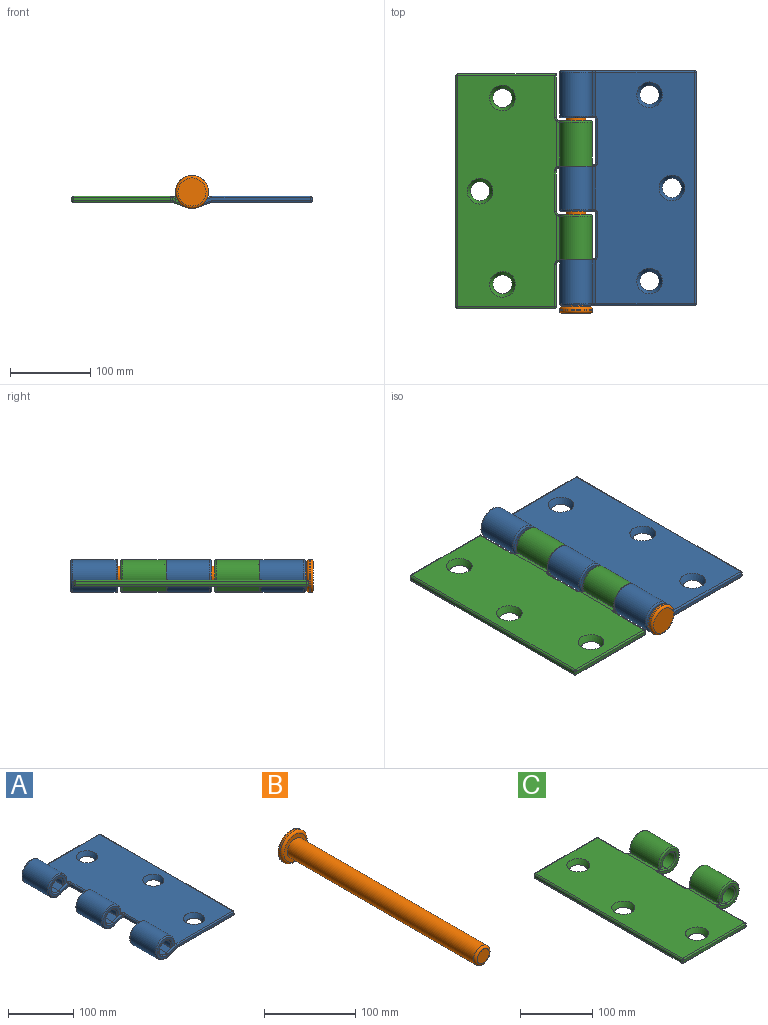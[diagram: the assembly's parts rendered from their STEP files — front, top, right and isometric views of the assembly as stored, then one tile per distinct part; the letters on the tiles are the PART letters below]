
ASSEMBLY  parts=3 mates=2
PART A: 95 faces, bbox 171.7x292x44.4 mm
  f0: plane 54.63x17.59mm, normal (0.34,0,-0.94), area 1016.4mm2, adj f2,f12,f42,f44,f80
  f1: plane 54.85x17.59mm, normal (0.34,0,-0.94), area 1016.5mm2, adj f3,f12,f51,f52,f62,f64
  f2: cylinder r=20.5mm len=54.4mm, axis (0,1,0), area 5913.6mm2, adj f0,f4,f40,f81
  f3: cylinder r=20.5mm len=54.4mm, axis (0,1,0), area 5913.6mm2, adj f1,f5,f49,f60
  f4: plane 54.4x8.42mm, normal (0,0,-1), area 458.3mm2, adj f2,f6,f38,f86
  f5: plane 54.4x8.42mm, normal (0,0,-1), area 458.3mm2, adj f3,f7,f47,f58
  f6: cylinder r=12.5mm len=54.4mm, axis (0,1,0), area 3703.3mm2, adj f4,f8,f36,f89
  f7: cylinder r=12.5mm len=54.4mm, axis (0,1,0), area 3703.3mm2, adj f5,f9,f45,f56
  f8: plane 55.3x20.54mm, normal (-0.32,0,0.95), area 1179mm2, adj f6,f10,f33,f34,f35,f92
  f9: plane 56.21x20.54mm, normal (-0.32,0,0.95), area 1179.8mm2, adj f7,f10,f39,f41,f43,f53,f54,f55
  f10: plane 288x123mm, normal (0,0,1), area 32774mm2, adj f8,f9,f17,f20,f21,f22,f35,f37
  f11: plane 288x4mm, normal (1,0,0), area 1152mm2, adj f83,f84,f90,f91
  f12: plane 288x123.06mm, normal (0,0,-1), area 33829.6mm2, adj f0,f1,f13,f20,f21,f22,f44,f46
  f13: plane 54.63x17.59mm, normal (0.34,0,-0.94), area 1016.4mm2, adj f12,f14,f71,f72,f75
  f14: cylinder r=20.5mm len=54.4mm, axis (0,1,0), area 5913.6mm2, adj f13,f15,f69,f73
  f15: plane 54.4x8.42mm, normal (0,0,-1), area 458.3mm2, adj f14,f16,f67,f74
  f16: cylinder r=12.5mm len=54.4mm, axis (0,1,0), area 3703.3mm2, adj f15,f17,f65,f76
  f17: plane 55.3x20.54mm, normal (-0.32,0,0.95), area 1179mm2, adj f10,f16,f59,f61,f63,f78
  f18: plane 166x37mm, normal (0,-1,0), area 913.5mm2, adj f80,f81,f85,f86,f89,f91,f92,f94
  f19: plane 166x37mm, normal (0,1,0), area 913.5mm2, adj f73,f74,f75,f76,f77,f78,f82,f83
  f20: cone r=16mm half-angle=26.6deg, axis (0,0,1), area 786.8mm2, adj f10,f12
  f21: cone r=16mm half-angle=26.6deg, axis (0,0,1), area 786.8mm2, adj f10,f12
  f22: cone r=16mm half-angle=26.6deg, axis (0,0,1), area 786.8mm2, adj f10,f12
  f23: plane 41x37mm, normal (0,1,0), area 413.9mm2, adj f29,f54,f56,f58,f60,f62
  f24: plane 54.4x4mm, normal (-1,0,0), area 217.6mm2, adj f29,f30,f57,f68
  f25: plane 41x37mm, normal (0,-1,0), area 413.9mm2, adj f30,f63,f65,f67,f69,f71
  f26: plane 41x37mm, normal (0,1,0), area 413.9mm2, adj f31,f34,f36,f38,f40,f42
  f27: plane 54.4x4mm, normal (-1,0,0), area 217.6mm2, adj f31,f32,f37,f48
  f28: plane 41x37mm, normal (0,-1,0), area 413.9mm2, adj f32,f43,f45,f47,f49,f51
  f29: cylinder r=2mm len=4.59mm, axis (0,0,1), area 12.3mm2, adj f23,f24,f53,f55,f64,f66
  f30: cylinder r=2mm len=4.59mm, axis (0,0,-1), area 12.3mm2, adj f24,f25,f59,f61,f70,f72
  f31: cylinder r=2mm len=4.59mm, axis (0,0,1), area 12.3mm2, adj f26,f27,f33,f35,f44,f46
  f32: cylinder r=2mm len=4.59mm, axis (0,0,-1), area 12.3mm2, adj f27,f28,f39,f41,f50,f52
  f33: bspline ~2.75x2.54mm, area 6mm2, adj f8,f31,f34,f35
  f34: cylinder r=2mm len=18.54mm, axis (-0.95,0,-0.32), area 59.3mm2, adj f8,f26,f33,f36
  f35: torus R=4mm, axis (0,0,-1), area 8.7mm2, adj f8,f10,f31,f33,f37
  f36: torus R=14.5mm, axis (0,1,0), area 222mm2, adj f6,f26,f34,f38
  f37: cylinder r=2mm len=54.4mm, axis (0,1,0), area 170.9mm2, adj f10,f27,f35,f39
  f38: cylinder r=2mm len=8.42mm, axis (1,0,0), area 19.6mm2, adj f4,f26,f36,f40
  f39: torus R=4mm, axis (0,0,-1), area 8.7mm2, adj f9,f10,f32,f37,f41
  f40: torus R=18.5mm, axis (0,1,0), area 326.9mm2, adj f2,f26,f38,f42
  f41: bspline ~3.65x3.11mm, area 6mm2, adj f9,f32,f39,f43
  f42: cylinder r=2mm len=16.94mm, axis (0.94,0,0.34), area 54.3mm2, adj f0,f26,f40,f44
  f43: cylinder r=2mm len=18.54mm, axis (0.95,0,0.32), area 59.3mm2, adj f9,f28,f41,f45
  f44: bspline ~2.47x2.33mm, area 3.5mm2, adj f0,f12,f31,f42,f46
  f45: torus R=14.5mm, axis (0,1,0), area 222mm2, adj f7,f28,f43,f47
  f46: torus R=4mm, axis (0,0,-1), area 9.2mm2, adj f12,f31,f44,f48
  f47: cylinder r=2mm len=8.42mm, axis (-1,0,0), area 19.6mm2, adj f5,f28,f45,f49
  f48: cylinder r=2mm len=54.4mm, axis (0,-1,0), area 170.9mm2, adj f12,f27,f46,f50
  f49: torus R=18.5mm, axis (0,1,0), area 326.9mm2, adj f3,f28,f47,f51
  f50: torus R=4mm, axis (0,0,-1), area 9.2mm2, adj f12,f32,f48,f52
  f51: cylinder r=2mm len=16.94mm, axis (-0.94,0,-0.34), area 54.3mm2, adj f1,f28,f49,f52
  f52: bspline ~2.47x2.33mm, area 3.5mm2, adj f1,f12,f32,f50,f51
  f53: bspline ~2.75x2.54mm, area 6mm2, adj f9,f29,f54,f55
  f54: cylinder r=2mm len=18.54mm, axis (-0.95,0,-0.32), area 59.3mm2, adj f9,f23,f53,f56
  f55: torus R=4mm, axis (0,0,-1), area 8.7mm2, adj f9,f10,f29,f53,f57
  f56: torus R=14.5mm, axis (0,1,0), area 222mm2, adj f7,f23,f54,f58
  f57: cylinder r=2mm len=54.4mm, axis (0,1,0), area 170.9mm2, adj f10,f24,f55,f59
  f58: cylinder r=2mm len=8.42mm, axis (1,0,0), area 19.6mm2, adj f5,f23,f56,f60
  f59: torus R=4mm, axis (0,0,-1), area 8.7mm2, adj f10,f17,f30,f57,f61
  f60: torus R=18.5mm, axis (0,1,0), area 326.9mm2, adj f3,f23,f58,f62
  f61: bspline ~3.65x3.11mm, area 6mm2, adj f17,f30,f59,f63
  f62: cylinder r=2mm len=16.94mm, axis (0.94,0,0.34), area 54.3mm2, adj f1,f23,f60,f64
  f63: cylinder r=2mm len=18.54mm, axis (0.95,0,0.32), area 59.3mm2, adj f17,f25,f61,f65
  f64: bspline ~2.47x2.33mm, area 3.5mm2, adj f1,f12,f29,f62,f66
  f65: torus R=14.5mm, axis (0,1,0), area 222mm2, adj f16,f25,f63,f67
  f66: torus R=4mm, axis (0,0,-1), area 9.2mm2, adj f12,f29,f64,f68
  f67: cylinder r=2mm len=8.42mm, axis (-1,0,0), area 19.6mm2, adj f15,f25,f65,f69
  f68: cylinder r=2mm len=54.4mm, axis (0,-1,0), area 170.9mm2, adj f12,f24,f66,f70
  f69: torus R=18.5mm, axis (0,1,0), area 326.9mm2, adj f14,f25,f67,f71
  f70: torus R=4mm, axis (0,0,-1), area 9.2mm2, adj f12,f30,f68,f72
  f71: cylinder r=2mm len=16.94mm, axis (-0.94,0,-0.34), area 54.3mm2, adj f13,f25,f69,f72
  f72: bspline ~2.47x2.33mm, area 3.5mm2, adj f12,f13,f30,f70,f71
  f73: torus R=18.5mm, axis (0,-1,0), area 326.9mm2, adj f14,f19,f74,f75
  f74: cylinder r=2mm len=8.42mm, axis (-1,0,0), area 19.6mm2, adj f15,f19,f73,f76
  f75: cylinder r=2mm len=18.59mm, axis (-0.94,0,-0.34), area 59.2mm2, adj f13,f19,f73,f77
  f76: torus R=14.5mm, axis (0,-1,0), area 222mm2, adj f16,f19,f74,f78
  f77: cylinder r=2mm len=123.35mm, axis (-1,0,0), area 387mm2, adj f12,f19,f75,f79
  f78: cylinder r=2mm len=21.18mm, axis (0.95,0,0.32), area 67.5mm2, adj f17,f19,f76,f82
  f79: sphere r=2mm, area 4mm2, adj f77,f83,f84
  f80: cylinder r=2mm len=18.59mm, axis (0.94,0,0.34), area 59.2mm2, adj f0,f18,f81,f85
  f81: torus R=18.5mm, axis (0,-1,0), area 326.9mm2, adj f2,f18,f80,f86
  f82: cylinder r=2mm len=123mm, axis (1,0,0), area 385.9mm2, adj f10,f19,f78,f87
  f83: cylinder r=2mm len=4mm, axis (0,0,-1), area 12.6mm2, adj f11,f19,f79,f87
  f84: cylinder r=2mm len=288mm, axis (0,-1,0), area 904.8mm2, adj f11,f12,f79,f88
  f85: cylinder r=2mm len=123.35mm, axis (1,0,0), area 387mm2, adj f12,f18,f80,f88
  f86: cylinder r=2mm len=8.42mm, axis (1,0,0), area 19.6mm2, adj f4,f18,f81,f89
  f87: sphere r=2mm, area 6.3mm2, adj f82,f83,f90
  f88: sphere r=2mm, area 6.3mm2, adj f84,f85,f91
  f89: torus R=14.5mm, axis (0,-1,0), area 222mm2, adj f6,f18,f86,f92
  f90: cylinder r=2mm len=288mm, axis (0,1,0), area 904.8mm2, adj f10,f11,f87,f93
  f91: cylinder r=2mm len=4mm, axis (0,0,1), area 12.6mm2, adj f11,f18,f88,f93
  f92: cylinder r=2mm len=21.18mm, axis (-0.95,0,-0.32), area 67.5mm2, adj f8,f18,f89,f94
  f93: sphere r=2mm, area 6.3mm2, adj f90,f91,f94
  f94: cylinder r=2mm len=123mm, axis (-1,0,0), area 385.9mm2, adj f10,f18,f92,f93
PART B: 8 faces, bbox 44.4x300x44.4 mm
  f0: cylinder r=12.25mm len=289mm, axis (0,1,0), area 22244mm2, adj f4,f7
  f1: plane 18.5x18.5mm, normal (0,-1,0), area 268.8mm2, adj f7
  f2: cylinder r=20.5mm len=41mm, axis (0,-1,0), area 257.6mm2, adj f5,f6
  f3: plane 35x35mm, normal (0,1,0), area 962.1mm2, adj f6
  f4: plane 35x35mm, normal (0,-1,0), area 490.7mm2, adj f0,f5
  f5: torus R=17.5mm, axis (0,1,0), area 574.7mm2, adj f2,f4
  f6: torus R=17.5mm, axis (0,1,0), area 574.7mm2, adj f2,f3
  f7: torus R=9.25mm, axis (0,1,0), area 330.4mm2, adj f0,f1
PART C: 85 faces, bbox 172x292.3x44.6 mm
  f0: plane 58.5x20.63mm, normal (0.32,0,0.95), area 1184.5mm2, adj f8,f12,f37,f40,f43,f65,f66,f67
  f1: plane 58.5x20.63mm, normal (0.32,0,0.95), area 1184.5mm2, adj f9,f12,f30,f32,f35,f71,f73,f75
  f2: plane 56.41x17.59mm, normal (-0.34,0,-0.94), area 1018.6mm2, adj f4,f14,f63,f64,f74,f76
  f3: plane 56.41x17.59mm, normal (-0.34,0,-0.94), area 1018.6mm2, adj f5,f14,f36,f39,f83,f84
  f4: cylinder r=20.5mm len=54.4mm, axis (0,1,0), area 5913.6mm2, adj f2,f6,f61,f72
  f5: cylinder r=20.5mm len=54.4mm, axis (0,1,0), area 5913.6mm2, adj f3,f7,f33,f81
  f6: plane 56.67x8.7mm, normal (0,0,-1), area 473.3mm2, adj f4,f8,f24,f34,f61,f70
  f7: plane 54.4x8.42mm, normal (0,0,-1), area 458.3mm2, adj f5,f9,f31,f79
  f8: cylinder r=12.5mm len=54.4mm, axis (0,1,0), area 3703.3mm2, adj f0,f6,f34,f68
  f9: cylinder r=12.5mm len=54.4mm, axis (0,1,0), area 3703.3mm2, adj f1,f7,f29,f77
  f10: plane 121x4mm, normal (0,-1,0), area 484mm2, adj f44,f45,f52,f53
  f11: plane 123x4mm, normal (0,1,0), area 492mm2, adj f23,f50,f56,f59
  f12: plane 288x123mm, normal (0,0,1), area 32676.1mm2, adj f0,f1,f15,f16,f17,f35,f38,f43
  f13: plane 288x4mm, normal (-1,0,0), area 1152mm2, adj f51,f52,f56,f57
  f14: plane 288x123.13mm, normal (0,0,-1), area 33731.7mm2, adj f2,f3,f15,f16,f17,f39,f42,f46
  f15: cone r=12mm half-angle=26.6deg, axis (0,0,1), area 786.8mm2, adj f12,f14
  f16: cone r=12mm half-angle=26.6deg, axis (0,0,1), area 786.8mm2, adj f12,f14
  f17: cone r=12mm half-angle=26.6deg, axis (0,0,1), area 786.8mm2, adj f12,f14
  f18: plane 52.4x4mm, normal (1,0,0), area 209.6mm2, adj f25,f38,f45,f46
  f19: plane 39x37mm, normal (0,-1,0), area 406.2mm2, adj f25,f29,f30,f31,f33,f36
  f20: plane 50.4x4mm, normal (1,0,0), area 201.6mm2, adj f26,f27,f69,f80
  f21: plane 39x37mm, normal (0,-1,0), area 406.2mm2, adj f26,f66,f68,f70,f72,f74
  f22: plane 39x37mm, normal (0,1,0), area 406.2mm2, adj f27,f75,f77,f79,f81,f83
  f23: plane 54.4x4mm, normal (1,0,0), area 217.6mm2, adj f11,f28,f47,f60
  f24: plane 39x37mm, normal (0,1,0), area 414.5mm2, adj f6,f28,f34,f37,f61,f63
  f25: cylinder r=4mm len=5.31mm, axis (0,0,-1), area 24.5mm2, adj f18,f19,f32,f35,f39,f42
  f26: cylinder r=4mm len=5.31mm, axis (0,0,-1), area 24.5mm2, adj f20,f21,f65,f67,f76,f78
  f27: cylinder r=4mm len=5.31mm, axis (0,0,1), area 24.5mm2, adj f20,f22,f71,f73,f82,f84
  f28: cylinder r=4mm len=5.31mm, axis (0,0,1), area 24.5mm2, adj f23,f24,f40,f43,f62,f64
  f29: torus R=14.5mm, axis (0,-1,0), area 222mm2, adj f9,f19,f30,f31
  f30: cylinder r=2mm len=16.54mm, axis (0.95,0,-0.32), area 52.7mm2, adj f1,f19,f29,f32
  f31: cylinder r=2mm len=8.42mm, axis (-1,0,0), area 19.6mm2, adj f7,f19,f29,f33
  f32: bspline ~4.48x3.39mm, area 12.2mm2, adj f1,f25,f30,f35
  f33: torus R=18.5mm, axis (0,-1,0), area 326.9mm2, adj f5,f19,f31,f36
  f34: torus R=14.5mm, axis (0,-1,0), area 225mm2, adj f6,f8,f24,f37
  f35: torus R=6mm, axis (0,0,-1), area 11.9mm2, adj f1,f12,f25,f32,f38
  f36: cylinder r=2mm len=14.94mm, axis (-0.94,0,0.34), area 47.6mm2, adj f3,f19,f33,f39
  f37: cylinder r=2mm len=16.54mm, axis (-0.95,0,0.32), area 52.7mm2, adj f0,f24,f34,f40
  f38: cylinder r=2mm len=52.4mm, axis (0,-1,0), area 164.6mm2, adj f12,f18,f35,f41
  f39: bspline ~4.33x3.19mm, area 10.4mm2, adj f3,f14,f25,f36,f42
  f40: bspline ~4.48x3.39mm, area 12.2mm2, adj f0,f28,f37,f43
  f41: sphere r=2mm, area 6.3mm2, adj f38,f44,f45
  f42: torus R=6mm, axis (0,0,1), area 13mm2, adj f14,f25,f39,f46
  f43: torus R=6mm, axis (0,0,-1), area 11.9mm2, adj f0,f12,f28,f40,f47
  f44: cylinder r=2mm len=121mm, axis (1,0,0), area 380.1mm2, adj f10,f12,f41,f48
  f45: cylinder r=2mm len=4mm, axis (0,0,1), area 12.6mm2, adj f10,f18,f41,f49
  f46: cylinder r=2mm len=52.4mm, axis (0,-1,0), area 164.6mm2, adj f14,f18,f42,f49
  f47: cylinder r=2mm len=54.4mm, axis (0,1,0), area 167.8mm2, adj f12,f23,f43,f50
  f48: sphere r=2mm, area 6.3mm2, adj f44,f51,f52
  f49: sphere r=2mm, area 8.6mm2, adj f45,f46,f53
  f50: cylinder r=2mm len=123mm, axis (-1,0,0), area 383.3mm2, adj f11,f12,f47,f54
  f51: cylinder r=2mm len=288mm, axis (0,1,0), area 904.8mm2, adj f12,f13,f48,f54
  f52: cylinder r=2mm len=4mm, axis (0,0,1), area 12.6mm2, adj f10,f13,f48,f55
  f53: cylinder r=2mm len=121mm, axis (-1,0,0), area 380.1mm2, adj f10,f14,f49,f55
  f54: sphere r=2mm, area 8.6mm2, adj f50,f51,f56
  f55: sphere r=2mm, area 6.3mm2, adj f52,f53,f57
  f56: cylinder r=2mm len=4mm, axis (0,0,-1), area 12.6mm2, adj f11,f13,f54,f58
  f57: cylinder r=2mm len=288mm, axis (0,1,0), area 904.8mm2, adj f13,f14,f55,f58
  f58: sphere r=2mm, area 6.3mm2, adj f56,f57,f59
  f59: cylinder r=2mm len=123mm, axis (1,0,0), area 383.3mm2, adj f11,f14,f58,f60
  f60: cylinder r=2mm len=54.4mm, axis (0,-1,0), area 167.8mm2, adj f14,f23,f59,f62
  f61: torus R=18.5mm, axis (0,-1,0), area 330.2mm2, adj f4,f6,f24,f63
  f62: torus R=6mm, axis (0,0,1), area 13mm2, adj f14,f28,f60,f64
  f63: cylinder r=2mm len=14.94mm, axis (0.94,0,-0.34), area 47.6mm2, adj f2,f24,f61,f64
  f64: bspline ~5.8x3.84mm, area 10.4mm2, adj f2,f14,f28,f62,f63
  f65: bspline ~4.48x3.39mm, area 12.2mm2, adj f0,f26,f66,f67
  f66: cylinder r=2mm len=16.54mm, axis (0.95,0,-0.32), area 52.7mm2, adj f0,f21,f65,f68
  f67: torus R=6mm, axis (0,0,-1), area 11.9mm2, adj f0,f12,f26,f65,f69
  f68: torus R=14.5mm, axis (0,-1,0), area 222mm2, adj f8,f21,f66,f70
  f69: cylinder r=2mm len=50.4mm, axis (0,1,0), area 158.3mm2, adj f12,f20,f67,f71
  f70: cylinder r=2mm len=8.42mm, axis (-1,0,0), area 19.6mm2, adj f6,f21,f68,f72
  f71: torus R=6mm, axis (0,0,-1), area 11.9mm2, adj f1,f12,f27,f69,f73
  f72: torus R=18.5mm, axis (0,-1,0), area 326.9mm2, adj f4,f21,f70,f74
  f73: bspline ~4.48x3.39mm, area 12.2mm2, adj f1,f27,f71,f75
  f74: cylinder r=2mm len=14.94mm, axis (-0.94,0,0.34), area 47.6mm2, adj f2,f21,f72,f76
  f75: cylinder r=2mm len=16.54mm, axis (-0.95,0,0.32), area 52.7mm2, adj f1,f22,f73,f77
  f76: bspline ~4.33x3.19mm, area 10.4mm2, adj f2,f14,f26,f74,f78
  f77: torus R=14.5mm, axis (0,-1,0), area 222mm2, adj f9,f22,f75,f79
  f78: torus R=6mm, axis (0,0,1), area 13mm2, adj f14,f26,f76,f80
  f79: cylinder r=2mm len=8.42mm, axis (1,0,0), area 19.6mm2, adj f7,f22,f77,f81
  f80: cylinder r=2mm len=50.4mm, axis (0,-1,0), area 158.3mm2, adj f14,f20,f78,f82
  f81: torus R=18.5mm, axis (0,-1,0), area 326.9mm2, adj f5,f22,f79,f83
  f82: torus R=6mm, axis (0,0,1), area 13mm2, adj f14,f27,f80,f84
  f83: cylinder r=2mm len=14.94mm, axis (0.94,0,-0.34), area 47.6mm2, adj f3,f22,f81,f84
  f84: bspline ~5.8x3.84mm, area 10.4mm2, adj f3,f14,f27,f82,f83
PLACE A t=(-168.2,-358.19,20.48)mm
PLACE B rot(axis=(1,0,0),180deg) t=(-168.2,-652.19,30.48)mm
PLACE C t=(-168.2,-362.19,20.48)mm
MATE slider B.f0 <-> A.f65  axis (0,1,0) through (-143.7,-360.19,25.48)mm
MATE revolute C.f4 <-> A.f2  axis (0,-1,0) through (-143.7,-593.79,25.48)mm
